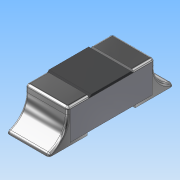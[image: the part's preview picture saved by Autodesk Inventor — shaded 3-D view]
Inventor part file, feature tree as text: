
AUTODESK INVENTOR PART (.ipt)
format: ipt  version: 2016 (Build 200138000, 138)  size: 207,360 bytes
history: native  units: mm
features: extrude x2, fillet x2, sketch x1, mirror x1
ambient origin geometry x8: Origin, YZ Plane, XZ Plane, XY Plane, X Axis, Y Axis, Z Axis, Center Point
bodies: Body1 (feature_tree)
feature tree (6):
  sketch  "Sketch10"  dims[d9=0.499mm d10=0.0mm d11=0.2mm d12=0.45mm d13=0.03mm d14=0.03mm d15=0.25mm d16=45.0deg d17=0.5mm d18=0.0mm d19=0.03mm d21=1.0mm d22=0.4mm d23=0.3mm d24=0.029mm]
  extrude  "Extrusion4"  Depth=0.2mm
  extrude  "Extrusion5"  Depth=0.45mm
  fillet  "Fillet2"  Radius=0.03mm
  fillet  "Fillet3"  Radius=0.03mm
  mirror  "Mirror1"
